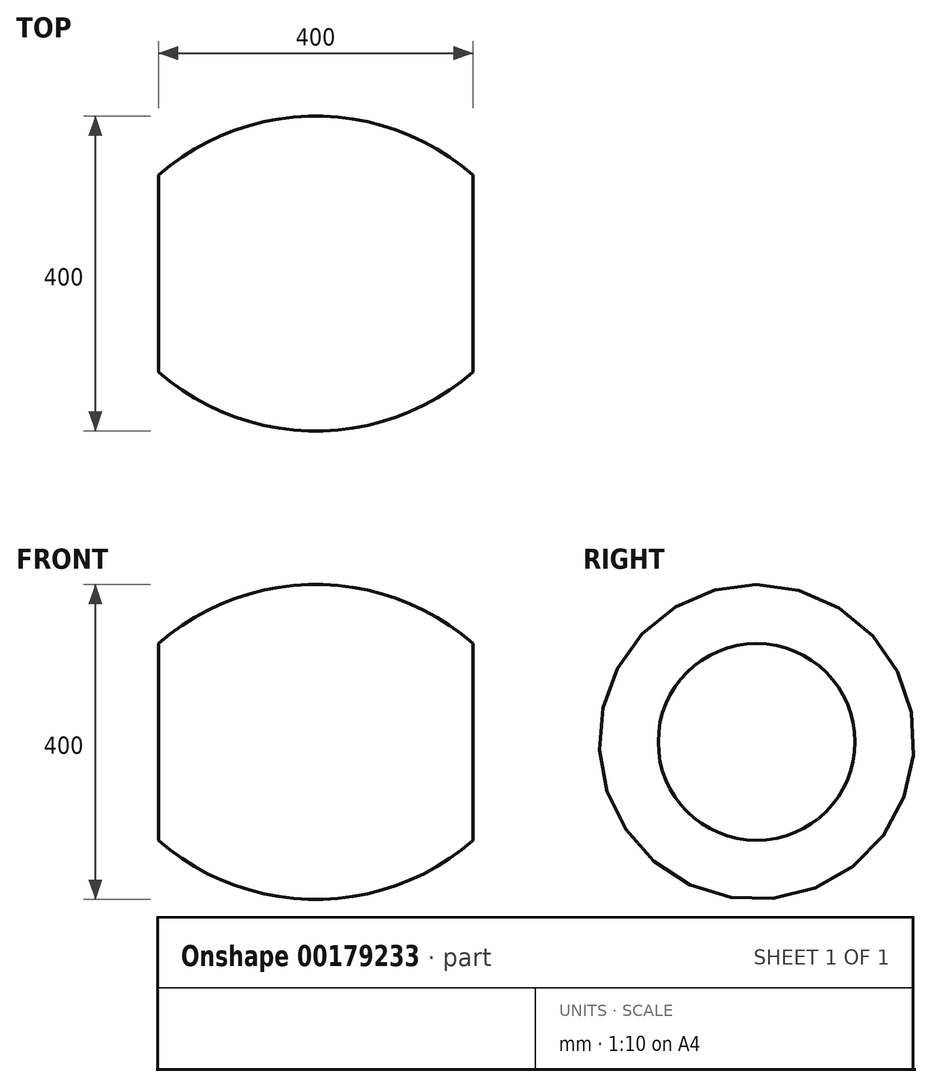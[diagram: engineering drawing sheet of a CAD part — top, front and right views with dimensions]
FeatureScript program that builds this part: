
annotation { "Feature Type Name" : "Feature", "Feature Type Description" : "" }
export const myFeature = defineFeature(function(context is Context, id is Id, definition is map)
    precondition{}
    {
        {
            var Q0;
            Q0=qCreatedBy(makeId("Front.planeOp"),FACE);
            var sketch = newSketch(context, id + "F0", { "sketchPlane" : qUnion([Q0])});
            skLineSegment(sketch, "E0", {"start": v(0, 0) * mm, "end": v(400, 0) * mm, "construction": true});
            skLineSegment(sketch, "E1", {"start": v(0, 0) * mm, "end": v(0, 125) * mm});
            skLineSegment(sketch, "E2", {"start": v(400, 0) * mm, "end": v(400, 125) * mm});
            skLineSegment(sketch, "E3", {"start": v(200, 0) * mm, "end": v(200, 200) * mm, "construction": true});
            skArc(sketch, "E4", {"start": v(400, 125) * mm, "mid": v(200, 200) * mm, "end": v(0, 125) * mm});
            skLineSegment(sketch, "E5", {"start": v(0, 0) * mm, "end": v(400, 0) * mm});
            skSolve(sketch);
        }
        {
            var Q0;
            Q0=makeQuery(id+"F0.imprint","IMPRINT",FACE,{"disambiguationData":[TD([[makeQuery(id+"F0.imprint","IMPRINT",EDGE,{"derivedFrom":sQuery(id+"F0.wireOp",EDGE,"E1")}),-1.0]])]});
            var Q1;
            Q1=sQuery(id+"F0.wireOp",EDGE,"E5");
            revolve(context, id + "F1", {"entities" : qUnion([Q0]), "axis" : qUnion([Q1]), "revolveType" : RevolveType.FULL});
        }
    });
